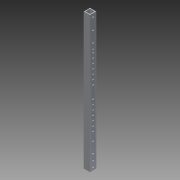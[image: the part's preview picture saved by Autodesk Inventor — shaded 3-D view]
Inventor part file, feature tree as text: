
AUTODESK INVENTOR PART (.ipt)
format: ipt  version: 2013 (Build 170138000, 138)  size: 223,744 bytes
history: native  units: in
note: dims shown in document units (in); Inventor stores cm internally (conversion verified against a paired STEP export)
features: extrude x4, sketch x4
ambient origin geometry x8: Origin, YZ Plane, XZ Plane, XY Plane, X Axis, Y Axis, Z Axis, Center Point
bodies: Solid1 (feature_tree)
feature tree (8):
  extrude  "Extrusion1"  Depth=1.0in
  extrude  "Extrusion2"  Depth=22.0in TaperAngle=0.0deg
  extrude  "Extrusion3"  Depth=0.26in
  extrude  "Extrusion4"  Depth=11.0236in
  sketch  "Sketch1"  dims[d0=1.0in d1=1.0in]
  sketch  "Sketch2"  dims[d2=0.125in d3=22.0in d4=0.0in]
  sketch  "Sketch3"  dims[d5=0.55in d6=0.26in]
  sketch  "Sketch4"  dims[d7=22.0in d8=11.0236in d10=0.7741in d11=0.3937in d13=1.0in d15=1.0in d16=0.0in d17=1.75in d18=2.0in d19=1.75in d20=1.75in d21=0.26in d22=0.26in d23=0.26in d24=0.26in d25=0.26in d26=0.26in d27=0.26in d28=0.26in d29=1.0in d30=0.0in d31=2.0in d32=0.26in d33=0.26in d40=0.5in d41=0.26in d42=0.5in d43=0.26in d46=0.75in d47=0.75in d48=0.26in d49=0.26in d50=1.0in d51=0.0in d52=0.26in d53=5.5in d64=1.0in d65=0.26in d66=0.55in d67=22.0in d68=11.0236in d70=0.7741in d71=0.3937in d73=1.0in d76=0.375in d77=0.375in d78=1.9685in d80=0.75in d81=0.3937in d83=1.0in d85=0.5in d86=2.3622in d88=0.75in d89=0.3937in d91=1.0in]
